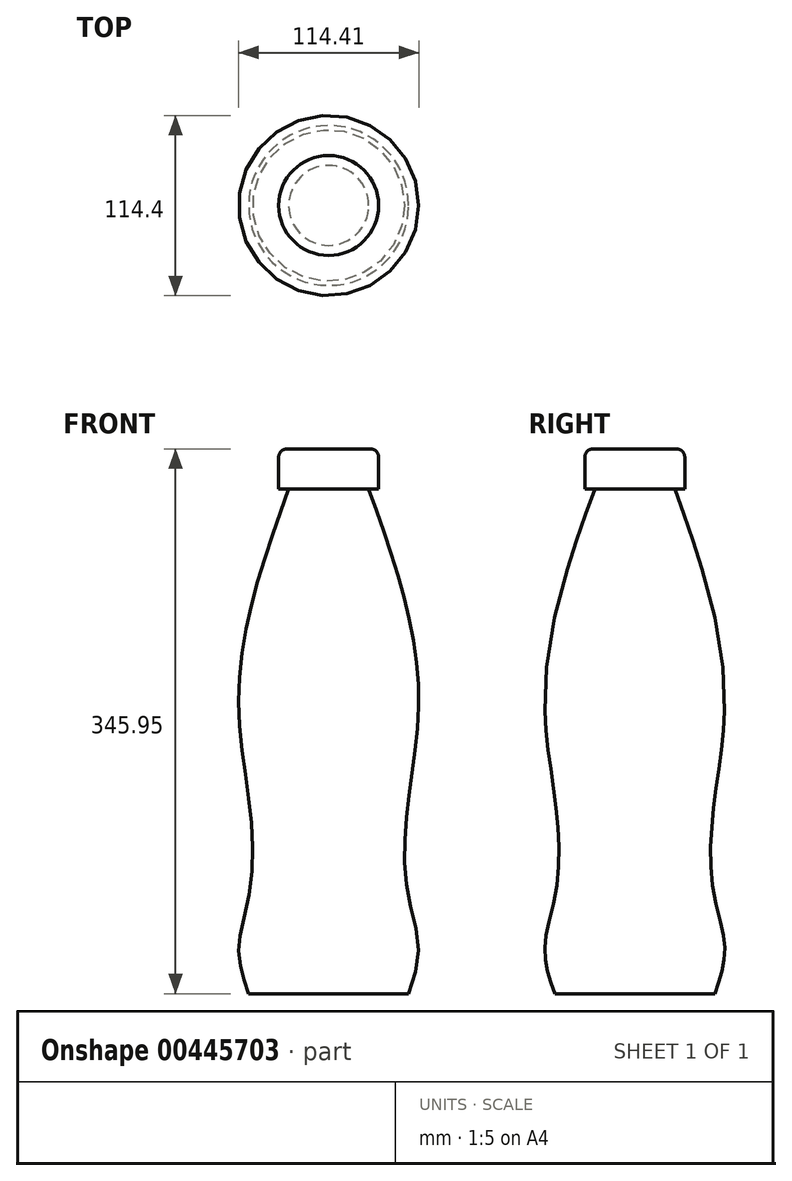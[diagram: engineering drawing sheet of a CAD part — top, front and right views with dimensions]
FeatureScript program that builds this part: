
annotation { "Feature Type Name" : "Feature", "Feature Type Description" : "" }
export const myFeature = defineFeature(function(context is Context, id is Id, definition is map)
    precondition{}
    {
        {
            var Q0;
            Q0=qCreatedBy(makeId("Top.planeOp"),FACE);
            cPlane(context, id + "F0", {"entities" : qUnion([Q0]), "cplaneType" : CPlaneType.OFFSET, "offset" : 25.9 * mm, "width" : 152.4 * mm, "height" : 152.4 * mm});
        }
        {
            var Q0;
            Q0=qCreatedBy(id+"F0.planeOp",FACE);
            cPlane(context, id + "F1", {"entities" : qUnion([Q0]), "cplaneType" : CPlaneType.OFFSET, "offset" : 35.05 * mm, "width" : 152.4 * mm, "height" : 152.4 * mm});
        }
        {
            var Q0;
            Q0=qCreatedBy(makeId("Top.planeOp"),FACE);
            var sketch = newSketch(context, id + "F2", { "sketchPlane" : qUnion([Q0])});
            skCircle(sketch, "E0", {"center": v(0, 0) * mm, "radius": 50.8 * mm});
            skSolve(sketch);
        }
        {
            var Q0;
            Q0=qCreatedBy(id+"F0.planeOp",FACE);
            var sketch = newSketch(context, id + "F3", { "sketchPlane" : qUnion([Q0])});
            skCircle(sketch, "E1", {"center": v(0, 0) * mm, "radius": 57.15 * mm});
            skSolve(sketch);
        }
        {
            var Q0;
            Q0=qCreatedBy(id+"F1.planeOp",FACE);
            var sketch = newSketch(context, id + "F4", { "sketchPlane" : qUnion([Q0])});
            skCircle(sketch, "E2", {"center": v(0, 0) * mm, "radius": 50.8 * mm});
            skSolve(sketch);
        }
        {
            var Q0;
            Q0=qCreatedBy(id+"F1.planeOp",FACE);
            cPlane(context, id + "F5", {"entities" : qUnion([Q0]), "cplaneType" : CPlaneType.OFFSET, "offset" : 120.9 * mm, "width" : 152.4 * mm, "height" : 152.4 * mm});
        }
        {
            var Q0;
            Q0=qCreatedBy(id+"F5.planeOp",FACE);
            var sketch = newSketch(context, id + "F6", { "sketchPlane" : qUnion([Q0])});
            skCircle(sketch, "E3", {"center": v(0, 0) * mm, "radius": 57.15 * mm});
            skSolve(sketch);
        }
        {
            var Q0;
            Q0=qCreatedBy(id+"F5.planeOp",FACE);
            cPlane(context, id + "F7", {"entities" : qUnion([Q0]), "cplaneType" : CPlaneType.OFFSET, "offset" : 138.68 * mm, "width" : 152.4 * mm, "height" : 152.4 * mm});
        }
        {
            var Q0;
            Q0=qCreatedBy(id+"F7.planeOp",FACE);
            var sketch = newSketch(context, id + "F8", { "sketchPlane" : qUnion([Q0])});
            skCircle(sketch, "E4", {"center": v(0, 0) * mm, "radius": 25.4 * mm});
            skSolve(sketch);
        }
        {
            var Q0;
            Q0=makeQuery(id+"F8.imprint","IMPRINT",FACE,{"disambiguationData":[TD([[makeQuery(id+"F8.imprint","IMPRINT",EDGE,{"derivedFrom":sQuery(id+"F8.wireOp",EDGE,"E4")}),1.0]])]});
            var Q1;
            Q1=makeQuery(id+"F6.imprint","IMPRINT",FACE,{"disambiguationData":[TD([[makeQuery(id+"F6.imprint","IMPRINT",EDGE,{"derivedFrom":sQuery(id+"F6.wireOp",EDGE,"E3")}),1.0]])]});
            var Q2;
            Q2=makeQuery(id+"F4.imprint","IMPRINT",FACE,{"disambiguationData":[TD([[makeQuery(id+"F4.imprint","IMPRINT",EDGE,{"derivedFrom":sQuery(id+"F4.wireOp",EDGE,"E2")}),1.0]])]});
            var Q3;
            Q3=makeQuery(id+"F3.imprint","IMPRINT",FACE,{"disambiguationData":[TD([[makeQuery(id+"F3.imprint","IMPRINT",EDGE,{"derivedFrom":sQuery(id+"F3.wireOp",EDGE,"E1")}),1.0]])]});
            var Q4;
            Q4=makeQuery(id+"F2.imprint","IMPRINT",FACE,{"disambiguationData":[TD([[makeQuery(id+"F2.imprint","IMPRINT",EDGE,{"derivedFrom":sQuery(id+"F2.wireOp",EDGE,"E0")}),1.0]])]});
            loft(context, id + "F9", {"sheetProfilesArray" : [{ "sheetProfileEntities" : qUnion([Q0]) }, { "sheetProfileEntities" : qUnion([Q1]) }, { "sheetProfileEntities" : qUnion([Q2]) }, { "sheetProfileEntities" : qUnion([Q3]) }, { "sheetProfileEntities" : qUnion([Q4]) }]});
        }
        {
            var Q0;
            Q0=qCreatedBy(id+"F7.planeOp",FACE);
            var sketch = newSketch(context, id + "F10", { "sketchPlane" : qUnion([Q0])});
            skCircle(sketch, "E5", {"center": v(0, 0) * mm, "radius": 31.75 * mm});
            skSolve(sketch);
        }
        {
            var Q0;
            Q0=qSketchRegion(id+"F10",true);
            extrude(context, id + "F11", {"entities" : qUnion([Q0]), "operationType" : NewBodyOperationType.ADD, "depth" : 25.4 * mm});
        }
        {
            var Q0;
            Q0=makeQuery(id+"F11.opExtrude","CAP_EDGE",EDGE,{"disambiguationData":[OSD([sQuery(id+"F10.wireOp",EDGE,"E5")])],"isStart":false});
            fillet(context, id + "F12", {"entities" : qUnion([Q0]), "radius" : 5.08 * mm, "tangentPropagation" : true, "allowEdgeOverflow" : false});
        }
        {
            var Q0;
            Q0=qCreatedBy(makeId("Right.planeOp"),FACE);
            var sketch = newSketch(context, id + "F13", { "sketchPlane" : qUnion([Q0])});
            skLineSegment(sketch, "E6", {"start": v(-82.2, 0) * mm, "end": v(111.65, 0) * mm, "construction": true});
            skSolve(sketch);
        }
    });
